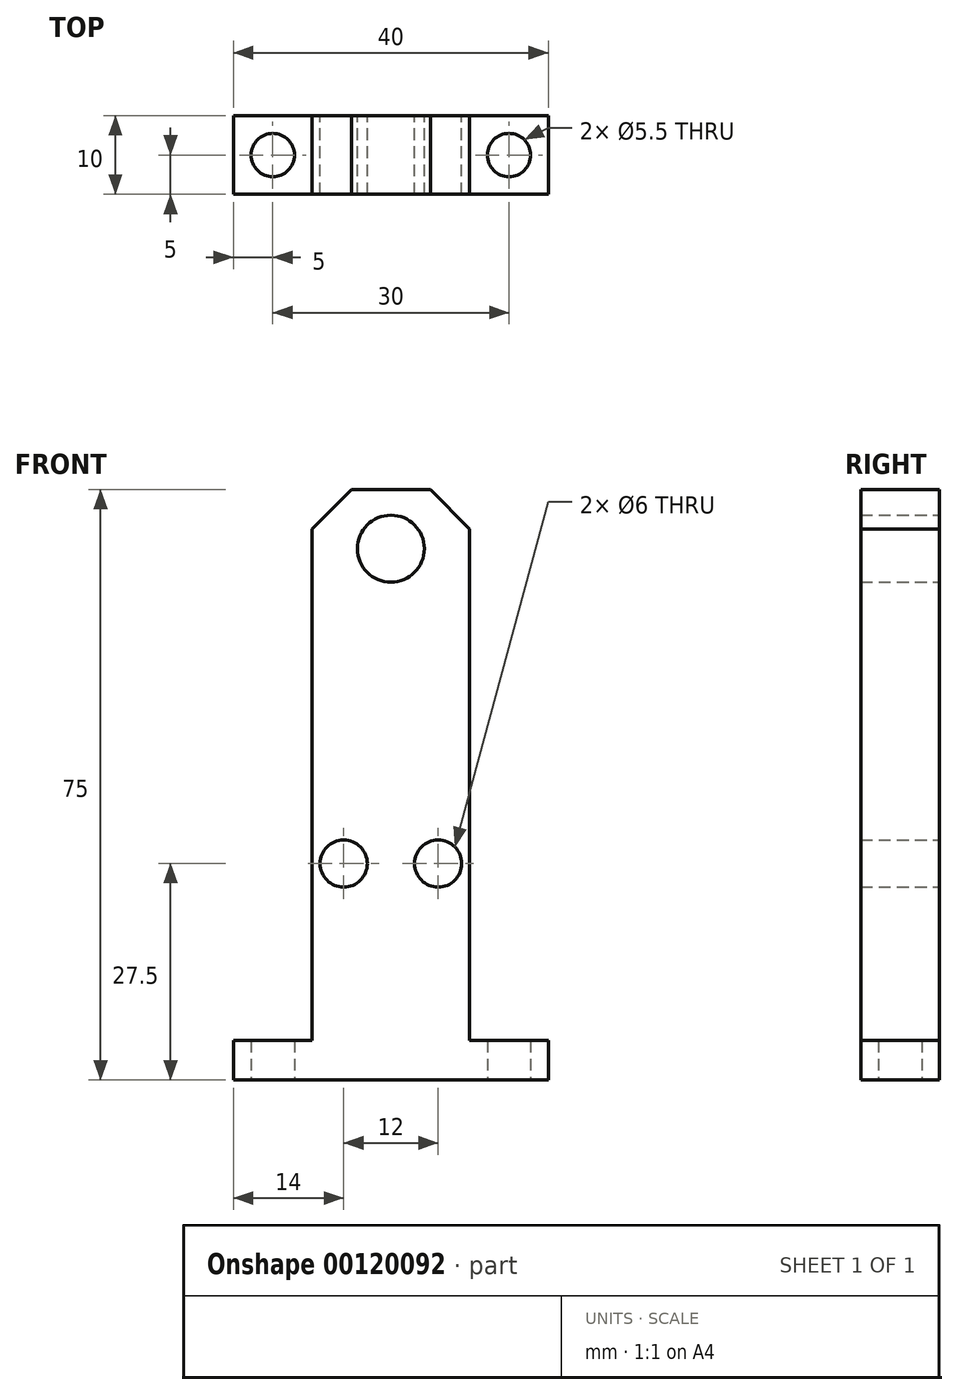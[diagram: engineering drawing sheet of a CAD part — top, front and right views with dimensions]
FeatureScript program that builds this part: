
annotation { "Feature Type Name" : "Feature", "Feature Type Description" : "" }
export const myFeature = defineFeature(function(context is Context, id is Id, definition is map)
    precondition{}
    {
        {
            var Q0;
            Q0=qCreatedBy(makeId("Front.planeOp"),FACE);
            var sketch = newSketch(context, id + "F0", { "sketchPlane" : qUnion([Q0])});
            skLineSegment(sketch, "E0.bottom", {"start": v(-10, 37.5) * mm, "end": v(10, 37.5) * mm});
            skLineSegment(sketch, "E0.top", {"start": v(-10, -37.5) * mm, "end": v(10, -37.5) * mm});
            skLineSegment(sketch, "E0.left", {"start": v(-10, 37.5) * mm, "end": v(-10, -37.5) * mm});
            skLineSegment(sketch, "E0.right", {"start": v(10, 37.5) * mm, "end": v(10, -37.5) * mm});
            skPoint(sketch, "E0.middle", {"position": v(0, 0) * mm});
            skLineSegment(sketch, "E1", {"start": v(0, 37.5) * mm, "end": v(0, 30) * mm});
            skPoint(sketch, "E1.endSnap0", {"position": v(0, 37.5) * mm});
            skCircle(sketch, "E2", {"center": v(0, 30) * mm, "radius": 4.25 * mm});
            skLineSegment(sketch, "E3", {"start": v(0, 30) * mm, "end": v(0, -10) * mm});
            skLineSegment(sketch, "E4", {"start": v(0, -10) * mm, "end": v(-6, -10) * mm});
            skCircle(sketch, "E5", {"center": v(-6, -10) * mm, "radius": 3 * mm});
            skLineSegment(sketch, "E6", {"start": v(0, -10) * mm, "end": v(6, -10) * mm});
            skCircle(sketch, "E7", {"center": v(6, -10) * mm, "radius": 3 * mm});
            skSolve(sketch);
        }
        {
            var Q0;
            Q0=makeQuery(id+"F0.imprint","IMPRINT",FACE,{"disambiguationData":[TD([[makeQuery(id+"F0.imprint","IMPRINT",EDGE,{"derivedFrom":sQuery(id+"F0.wireOp",EDGE,"E0.top")}),1.0]])]});
            extrude(context, id + "F1", {"entities" : qUnion([Q0]), "endBound" : BoundingType.SYMMETRIC, "depth" : 10 * mm});
        }
        {
            var Q0;
            Q0=makeQuery(id+"F1.opExtrude","SWEPT_EDGE",EDGE,{"disambiguationData":[OSD([sQuery(id+"F0.wireOp",EDGE,"E0.bottom"),sQuery(id+"F0.wireOp",EDGE,"E0.left")])]});
            var Q1;
            Q1=makeQuery(id+"F1.opExtrude","SWEPT_EDGE",EDGE,{"disambiguationData":[OSD([sQuery(id+"F0.wireOp",EDGE,"E0.bottom"),sQuery(id+"F0.wireOp",EDGE,"E0.right")])]});
            chamfer(context, id + "F2", {"entities" : qUnion([Q0, Q1]), "width" : 5 * mm, "tangentPropagation" : true});
        }
        {
            var Q0;
            Q0=makeQuery(id+"F1.opExtrude","SWEPT_FACE",FACE,{"disambiguationData":[OSD([sQuery(id+"F0.wireOp",EDGE,"E0.top")])]});
            var sketch = newSketch(context, id + "F3", { "sketchPlane" : qUnion([Q0])});
            skLineSegment(sketch, "E8.bottom", {"start": v(10, 5) * mm, "end": v(20, 5) * mm});
            skLineSegment(sketch, "E8.top", {"start": v(10, -5) * mm, "end": v(20, -5) * mm});
            skLineSegment(sketch, "E8.left", {"start": v(10, 5) * mm, "end": v(10, -5) * mm});
            skLineSegment(sketch, "E8.right", {"start": v(20, 5) * mm, "end": v(20, -5) * mm});
            skLineSegment(sketch, "E9", {"start": v(15, 5) * mm, "end": v(15, 0) * mm});
            skLineSegment(sketch, "E10.bottom", {"start": v(-10, 5) * mm, "end": v(-20, 5) * mm});
            skLineSegment(sketch, "E10.top", {"start": v(-10, -5) * mm, "end": v(-20, -5) * mm});
            skLineSegment(sketch, "E10.left", {"start": v(-10, 5) * mm, "end": v(-10, -5) * mm});
            skLineSegment(sketch, "E10.right", {"start": v(-20, 5) * mm, "end": v(-20, -5) * mm});
            skLineSegment(sketch, "E11", {"start": v(-15, 5) * mm, "end": v(-15, 0) * mm});
            skCircle(sketch, "E12", {"center": v(-15, 0) * mm, "radius": 2.75 * mm});
            skCircle(sketch, "E13", {"center": v(15, 0) * mm, "radius": 2.75 * mm});
            skSolve(sketch);
        }
        {
            var Q0;
            Q0=makeQuery(id+"F3.imprint","IMPRINT",FACE,{"disambiguationData":[TD([[makeQuery(id+"F3.imprint","IMPRINT",EDGE,{"derivedFrom":sQuery(id+"F3.wireOp",EDGE,"E10.top")}),-1.0]])]});
            var Q1;
            Q1=makeQuery(id+"F3.imprint","IMPRINT",FACE,{"disambiguationData":[TD([[makeQuery(id+"F3.imprint","IMPRINT",EDGE,{"derivedFrom":sQuery(id+"F3.wireOp",EDGE,"E8.top")}),1.0]])]});
            extrude(context, id + "F4", {"entities" : qUnion([Q0, Q1]), "operationType" : NewBodyOperationType.ADD, "oppositeDirection" : true, "depth" : 5 * mm});
        }
    });
